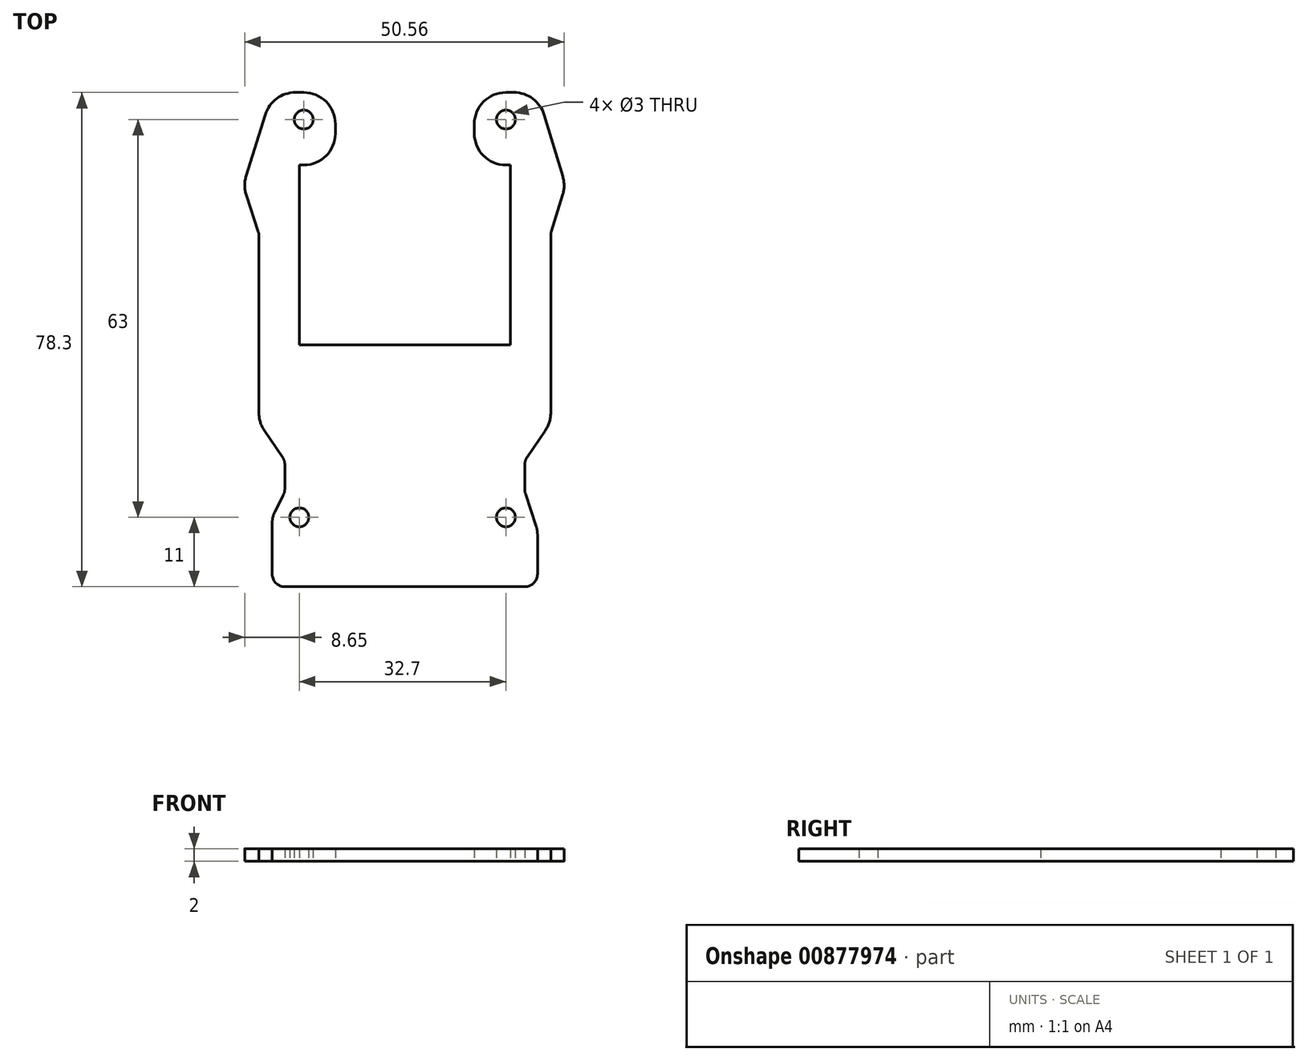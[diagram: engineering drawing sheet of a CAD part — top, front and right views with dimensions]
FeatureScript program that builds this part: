
annotation { "Feature Type Name" : "Feature", "Feature Type Description" : "" }
export const myFeature = defineFeature(function(context is Context, id is Id, definition is map)
    precondition{}
    {
        {
            var Q0;
            Q0=qCreatedBy(makeId("Top.planeOp"),FACE);
            var sketch = newSketch(context, id + "F0", { "sketchPlane" : qUnion([Q0])});
            skLineSegment(sketch, "E0", {"start": v(-16.7, -0.85) * mm, "end": v(-16.7, 27.65) * mm});
            skLineSegment(sketch, "E1", {"start": v(-16.7, 27.65) * mm, "end": v(-11, 27.65) * mm});
            skLineSegment(sketch, "E2", {"start": v(-11, 27.65) * mm, "end": v(-11, 39.15) * mm});
            skLineSegment(sketch, "E3", {"start": v(-21, 39.15) * mm, "end": v(-25.6, 24.35) * mm});
            skLineSegment(sketch, "E4", {"start": v(-25.6, 24.35) * mm, "end": v(-23.1, 16.82) * mm});
            skLineSegment(sketch, "E5", {"start": v(-23.1, 16.82) * mm, "end": v(-23.1, -13.15) * mm});
            skLineSegment(sketch, "E6", {"start": v(-19, -24.15) * mm, "end": v(-21, -28.15) * mm});
            skLineSegment(sketch, "E7", {"start": v(-21, -28.15) * mm, "end": v(-21, -39.15) * mm});
            skLineSegment(sketch, "E8", {"start": v(-21, -39.15) * mm, "end": v(21, -39.15) * mm});
            skLineSegment(sketch, "E9", {"start": v(-19, -24.15) * mm, "end": v(-19, -19.15) * mm});
            skLineSegment(sketch, "E10", {"start": v(-19, -19.15) * mm, "end": v(-23.1, -13.15) * mm});
            skLineSegment(sketch, "E11", {"start": v(-16.7, -0.85) * mm, "end": v(16.7, -0.85) * mm});
            skLineSegment(sketch, "E12", {"start": v(16.7, -0.85) * mm, "end": v(16.7, 27.65) * mm});
            skLineSegment(sketch, "E13", {"start": v(16.7, 27.65) * mm, "end": v(11, 27.65) * mm});
            skLineSegment(sketch, "E14", {"start": v(11, 27.65) * mm, "end": v(11, 39.15) * mm});
            skLineSegment(sketch, "E15", {"start": v(11, 39.15) * mm, "end": v(21, 39.15) * mm});
            skLineSegment(sketch, "E16", {"start": v(21, 39.15) * mm, "end": v(25.44, 24.35) * mm});
            skLineSegment(sketch, "E17", {"start": v(25.44, 24.35) * mm, "end": v(23.1, 16.82) * mm});
            skLineSegment(sketch, "E18", {"start": v(23.1, 16.82) * mm, "end": v(23.1, -13.15) * mm});
            skLineSegment(sketch, "E19", {"start": v(23.1, -13.15) * mm, "end": v(19, -19.15) * mm});
            skLineSegment(sketch, "E20", {"start": v(19, -19.15) * mm, "end": v(19, -24.15) * mm});
            skLineSegment(sketch, "E21", {"start": v(19, -24.15) * mm, "end": v(21, -30.17) * mm});
            skLineSegment(sketch, "E22", {"start": v(21, -30.17) * mm, "end": v(21, -39.15) * mm});
            skLineSegment(sketch, "E23", {"start": v(-21, 39.15) * mm, "end": v(-11, 39.15) * mm});
            skCircle(sketch, "E24", {"center": v(16, 34.85) * mm, "radius": 1.5 * mm});
            skCircle(sketch, "E25", {"center": v(-16, 34.85) * mm, "radius": 1.5 * mm});
            skCircle(sketch, "E26", {"center": v(-16.7, -28.15) * mm, "radius": 1.5 * mm});
            skCircle(sketch, "E27", {"center": v(16, -28.15) * mm, "radius": 1.5 * mm});
            skSolve(sketch);
        }
        {
            var Q0;
            Q0=qSketchRegion(id+"F0",true);
            extrude(context, id + "F1", {"entities" : qUnion([Q0]), "depth" : 2 * mm, "offsetDistance" : 25 * mm});
        }
        {
            var Q0;
            Q0=makeQuery(id+"F1.opExtrude","SWEPT_EDGE",EDGE,{"disambiguationData":[OSD([sQuery(id+"F0.wireOp",EDGE,"E1"),sQuery(id+"F0.wireOp",EDGE,"E2")])]});
            var Q1;
            Q1=makeQuery(id+"F1.opExtrude","SWEPT_EDGE",EDGE,{"disambiguationData":[OSD([sQuery(id+"F0.wireOp",EDGE,"E13"),sQuery(id+"F0.wireOp",EDGE,"E14")])]});
            var Q2;
            Q2=makeQuery(id+"F1.opExtrude","SWEPT_EDGE",EDGE,{"disambiguationData":[OSD([sQuery(id+"F0.wireOp",EDGE,"E14"),sQuery(id+"F0.wireOp",EDGE,"E15")])]});
            var Q3;
            Q3=makeQuery(id+"F1.opExtrude","SWEPT_EDGE",EDGE,{"disambiguationData":[OSD([sQuery(id+"F0.wireOp",EDGE,"E15"),sQuery(id+"F0.wireOp",EDGE,"E16")])]});
            var Q4;
            Q4=makeQuery(id+"F1.opExtrude","SWEPT_EDGE",EDGE,{"disambiguationData":[OSD([sQuery(id+"F0.wireOp",EDGE,"E2"),sQuery(id+"F0.wireOp",EDGE,"E23")])]});
            var Q5;
            Q5=makeQuery(id+"F1.opExtrude","SWEPT_EDGE",EDGE,{"disambiguationData":[OSD([sQuery(id+"F0.wireOp",EDGE,"E3"),sQuery(id+"F0.wireOp",EDGE,"E23")])]});
            var Q6;
            Q6=makeQuery(id+"F1.opExtrude","SWEPT_EDGE",EDGE,{"disambiguationData":[OSD([sQuery(id+"F0.wireOp",EDGE,"E3"),sQuery(id+"F0.wireOp",EDGE,"E4")])]});
            var Q7;
            Q7=makeQuery(id+"F1.opExtrude","SWEPT_EDGE",EDGE,{"disambiguationData":[OSD([sQuery(id+"F0.wireOp",EDGE,"E16"),sQuery(id+"F0.wireOp",EDGE,"E17")])]});
            var Q8;
            Q8=makeQuery(id+"F1.opExtrude","SWEPT_EDGE",EDGE,{"disambiguationData":[OSD([sQuery(id+"F0.wireOp",EDGE,"E18"),sQuery(id+"F0.wireOp",EDGE,"E19")])]});
            var Q9;
            Q9=makeQuery(id+"F1.opExtrude","SWEPT_EDGE",EDGE,{"disambiguationData":[OSD([sQuery(id+"F0.wireOp",EDGE,"E5"),sQuery(id+"F0.wireOp",EDGE,"E10")])]});
            fillet(context, id + "F2", {"entities" : qUnion([Q0, Q1, Q2, Q3, Q4, Q5, Q6, Q7, Q8, Q9]), "radius" : 5 * mm, "tangentPropagation" : true, "allowEdgeOverflow" : false});
        }
        {
            var Q0;
            Q0=makeQuery(id+"F1.opExtrude","SWEPT_EDGE",EDGE,{"disambiguationData":[OSD([sQuery(id+"F0.wireOp",EDGE,"E17"),sQuery(id+"F0.wireOp",EDGE,"E18")])]});
            var Q1;
            Q1=makeQuery(id+"F1.opExtrude","SWEPT_EDGE",EDGE,{"disambiguationData":[OSD([sQuery(id+"F0.wireOp",EDGE,"E4"),sQuery(id+"F0.wireOp",EDGE,"E5")])]});
            var Q2;
            Q2=makeQuery(id+"F1.opExtrude","SWEPT_EDGE",EDGE,{"disambiguationData":[OSD([sQuery(id+"F0.wireOp",EDGE,"E9"),sQuery(id+"F0.wireOp",EDGE,"E10")])]});
            var Q3;
            Q3=makeQuery(id+"F1.opExtrude","SWEPT_EDGE",EDGE,{"disambiguationData":[OSD([sQuery(id+"F0.wireOp",EDGE,"E6"),sQuery(id+"F0.wireOp",EDGE,"E9")])]});
            var Q4;
            Q4=makeQuery(id+"F1.opExtrude","SWEPT_EDGE",EDGE,{"disambiguationData":[OSD([sQuery(id+"F0.wireOp",EDGE,"E19"),sQuery(id+"F0.wireOp",EDGE,"E20")])]});
            var Q5;
            Q5=makeQuery(id+"F1.opExtrude","SWEPT_EDGE",EDGE,{"disambiguationData":[OSD([sQuery(id+"F0.wireOp",EDGE,"E20"),sQuery(id+"F0.wireOp",EDGE,"E21")])]});
            var Q6;
            Q6=makeQuery(id+"F1.opExtrude","SWEPT_EDGE",EDGE,{"disambiguationData":[OSD([sQuery(id+"F0.wireOp",EDGE,"E8"),sQuery(id+"F0.wireOp",EDGE,"E22")])]});
            var Q7;
            Q7=makeQuery(id+"F1.opExtrude","SWEPT_EDGE",EDGE,{"disambiguationData":[OSD([sQuery(id+"F0.wireOp",EDGE,"E7"),sQuery(id+"F0.wireOp",EDGE,"E8")])]});
            fillet(context, id + "F3", {"entities" : qUnion([Q0, Q1, Q2, Q3, Q4, Q5, Q6, Q7]), "radius" : 2 * mm, "tangentPropagation" : true, "allowEdgeOverflow" : false});
        }
        {
            var Q0;
            Q0=makeQuery(id+"F1.opExtrude","SWEPT_EDGE",EDGE,{"disambiguationData":[OSD([sQuery(id+"F0.wireOp",EDGE,"E6"),sQuery(id+"F0.wireOp",EDGE,"E7")])]});
            var Q1;
            Q1=makeQuery(id+"F1.opExtrude","SWEPT_EDGE",EDGE,{"disambiguationData":[OSD([sQuery(id+"F0.wireOp",EDGE,"E21"),sQuery(id+"F0.wireOp",EDGE,"E22")])]});
            fillet(context, id + "F4", {"entities" : qUnion([Q0, Q1]), "radius" : 4 * mm, "tangentPropagation" : true, "allowEdgeOverflow" : false});
        }
    });
